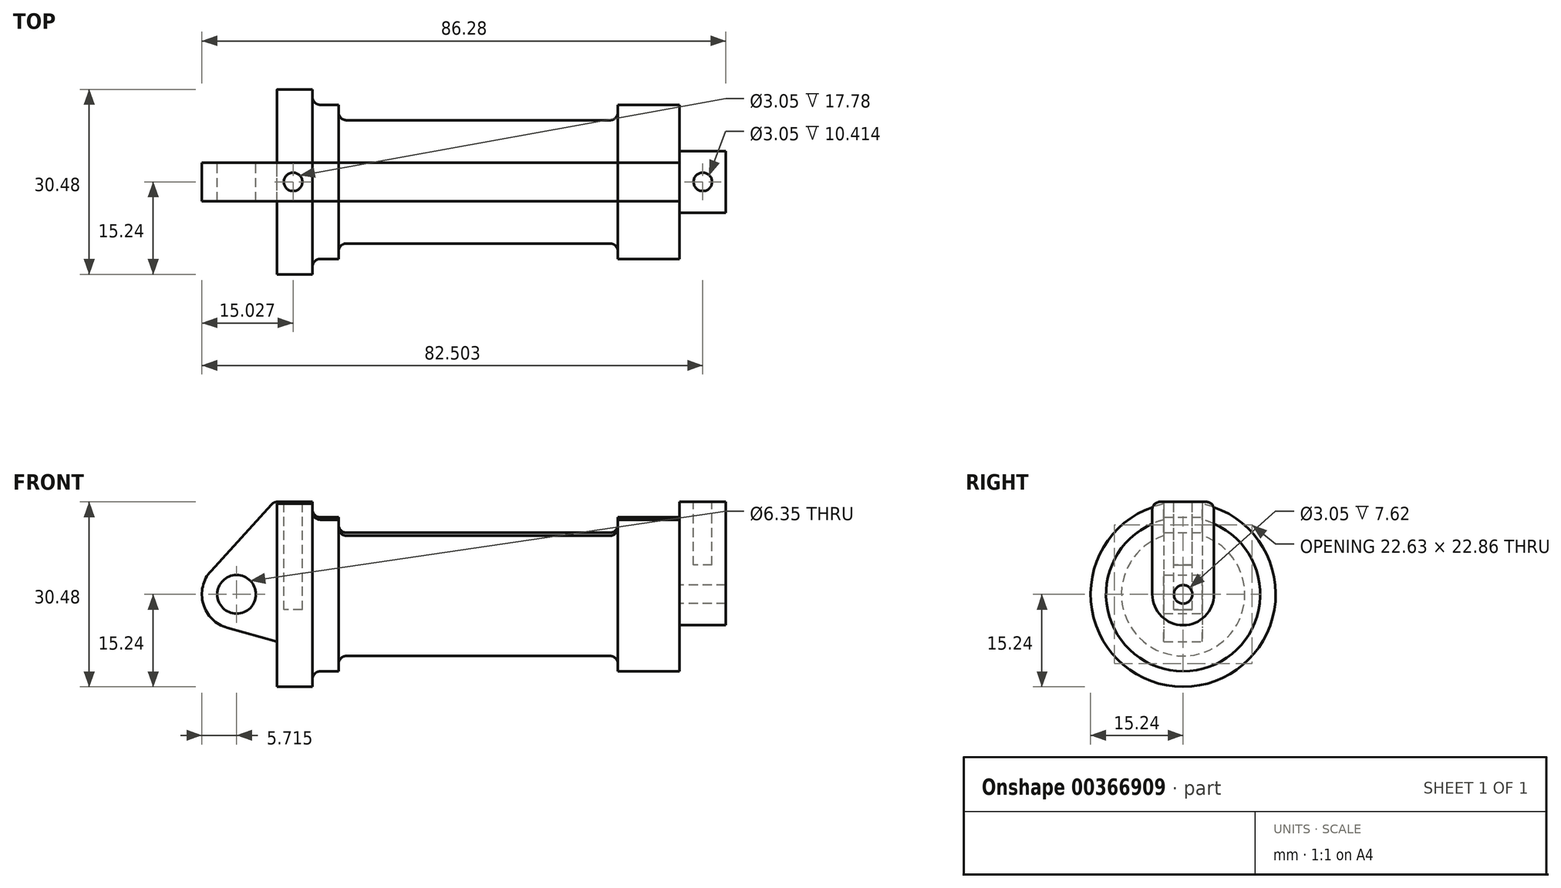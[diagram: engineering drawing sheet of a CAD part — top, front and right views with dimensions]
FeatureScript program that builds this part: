
annotation { "Feature Type Name" : "Feature", "Feature Type Description" : "" }
export const myFeature = defineFeature(function(context is Context, id is Id, definition is map)
    precondition{}
    {
        {
            var Q0;
            Q0=qCreatedBy(makeId("Front.planeOp"),FACE);
            var sketch = newSketch(context, id + "F0", { "sketchPlane" : qUnion([Q0])});
            skLineSegment(sketch, "E0", {"start": v(0, 0) * mm, "end": v(0, 15.25) * mm});
            skLineSegment(sketch, "E1", {"start": v(7.11, 12.7) * mm, "end": v(10.16, 12.7) * mm});
            skLineSegment(sketch, "E2", {"start": v(10.16, 12.7) * mm, "end": v(10.16, 11.43) * mm});
            skLineSegment(sketch, "E3", {"start": v(11.43, 10.16) * mm, "end": v(54.86, 10.16) * mm});
            skLineSegment(sketch, "E4", {"start": v(56.13, 11.43) * mm, "end": v(56.13, 12.7) * mm});
            skLineSegment(sketch, "E5", {"start": v(56.13, 12.7) * mm, "end": v(66.3, 12.7) * mm});
            skLineSegment(sketch, "E6", {"start": v(66.3, 12.7) * mm, "end": v(66.3, 0) * mm});
            skLineSegment(sketch, "E7", {"start": v(66.3, 0) * mm, "end": v(7.11, 0) * mm});
            skLineSegment(sketch, "E8", {"start": v(5.84, 15.24) * mm, "end": v(0.05, 15.24) * mm});
            skLineSegment(sketch, "E9", {"start": v(-0.89, 14.83) * mm, "end": v(-10.88, 3.85) * mm});
            skLineSegment(sketch, "E10", {"start": v(0, 0) * mm, "end": v(-6.65, 0) * mm});
            skCircle(sketch, "E11", {"center": v(-6.65, 0) * mm, "radius": 5.72 * mm});
            skCircle(sketch, "E12", {"center": v(-6.65, 0) * mm, "radius": 3.18 * mm});
            skLineSegment(sketch, "E13", {"start": v(5.84, 15.24) * mm, "end": v(5.84, 13.97) * mm});
            skLineSegment(sketch, "E14", {"start": v(4.23, -8.95) * mm, "end": v(-8.18, -5.5) * mm});
            skPoint(sketch, "E15.newPointA", {"position": v(5.84, -9.4) * mm});
            skPoint(sketch, "E16.visualSharp", {"position": v(10.16, 10.16) * mm});
            skLineSegment(sketch, "E17", {"start": v(5.84, -7.73) * mm, "end": v(5.84, -1.27) * mm});
            skPoint(sketch, "E18.visualSharp", {"position": v(5.84, 12.7) * mm});
            skArc(sketch, "E18.filletArc", {"start": v(5.84, 13.97) * mm, "mid": v(6.21, 13.07) * mm, "end": v(7.11, 12.7) * mm});
            skArc(sketch, "E19.filletArc", {"start": v(10.16, 11.43) * mm, "mid": v(10.53, 10.53) * mm, "end": v(11.43, 10.16) * mm});
            skArc(sketch, "E20.filletArc", {"start": v(7.11, 0) * mm, "mid": v(6.21, -0.37) * mm, "end": v(5.84, -1.27) * mm});
            skPoint(sketch, "E21.visualSharp", {"position": v(56.13, 10.16) * mm});
            skArc(sketch, "E21.filletArc", {"start": v(54.86, 10.16) * mm, "mid": v(55.76, 10.53) * mm, "end": v(56.13, 11.43) * mm});
            skLineSegment(sketch, "E22", {"start": v(7.11, 0) * mm, "end": v(0, 0) * mm});
            skArc(sketch, "E23.filletArc", {"start": v(4.23, -8.95) * mm, "mid": v(5.34, -8.74) * mm, "end": v(5.84, -7.73) * mm});
            skPoint(sketch, "E24.visualSharp", {"position": v(-0.5, 15.24) * mm});
            skArc(sketch, "E24.filletArc", {"start": v(0.05, 15.24) * mm, "mid": v(-0.46, 15.13) * mm, "end": v(-0.89, 14.83) * mm});
            skSolve(sketch);
        }
        {
            var Q0;
            Q0=makeQuery(id+"F0.imprint","IMPRINT",FACE,{"disambiguationData":[TD([[makeQuery(id+"F0.imprint","IMPRINT",EDGE,{"derivedFrom":sQuery(id+"F0.wireOp",EDGE,"E1")}),-1.0]])]});
            var Q1;
            Q1=sQuery(id+"F0.wireOp",EDGE,"E7");
            revolve(context, id + "F1", {"entities" : qUnion([Q0]), "axis" : qUnion([Q1]), "revolveType" : RevolveType.FULL});
        }
        {
            var Q0;
            {var subQ1=sQuery(id+"F0.wireOp",EDGE,"E0");Q0=makeQuery(id+"F0.imprint","IMPRINT",FACE,{"disambiguationData":[TD([[makeQuery(id+"F0.imprint","IMPRINT",EDGE,{"derivedFrom":subQ1}),1.0]])]});}
            var Q1;
            {var subQ0=sQuery(id+"F0.wireOp",EDGE,"E0");Q1=makeQuery(id+"F0.imprint","IMPRINT",FACE,{"disambiguationData":[TD([[makeQuery(id+"F0.imprint","IMPRINT",EDGE,{"derivedFrom":subQ0}),-1.0]])]});}
            var Q2;
            {var subQ0=sQuery(id+"F0.wireOp",EDGE,"E14");Q2=makeQuery(id+"F0.imprint","IMPRINT",FACE,{"disambiguationData":[TD([[makeQuery(id+"F0.imprint","IMPRINT",EDGE,{"derivedFrom":subQ0}),-1.0]])]});}
            var Q3;
            {var subQ5=sQuery(id+"F0.wireOp",EDGE,"E12");Q3=makeQuery(id+"F0.imprint","IMPRINT",FACE,{"disambiguationData":[TD([[makeQuery(id+"F0.imprint","IMPRINT",EDGE,{"derivedFrom":subQ5}),-1.0]])]});}
            extrude(context, id + "F2", {"entities" : qUnion([Q0, Q1, Q2, Q3]), "operationType" : NewBodyOperationType.ADD, "endBound" : BoundingType.SYMMETRIC, "depth" : 6.35 * mm});
        }
        {
            var Q0;
            Q0=makeQuery(id+"F1.opRevolve","SWEPT_FACE",FACE,{"disambiguationData":[OSD([sQuery(id+"F0.wireOp",EDGE,"E6")])]});
            var sketch = newSketch(context, id + "F3", { "sketchPlane" : qUnion([Q0])});
            skCircle(sketch, "E25", {"center": v(0, 0) * mm, "radius": 1.52 * mm});
            skCircle(sketch, "E26", {"center": v(0, 0) * mm, "radius": 5.08 * mm});
            skLineSegment(sketch, "E27", {"start": v(-5.08, 0) * mm, "end": v(-5.08, 13.97) * mm});
            skLineSegment(sketch, "E28", {"start": v(5.08, 0) * mm, "end": v(5.08, 13.97) * mm});
            skLineSegment(sketch, "E29", {"start": v(-3.81, 15.24) * mm, "end": v(3.81, 15.24) * mm});
            skPoint(sketch, "E30.visualSharp", {"position": v(-5.08, 15.24) * mm});
            skArc(sketch, "E30.filletArc", {"start": v(-3.81, 15.24) * mm, "mid": v(-4.7, 14.87) * mm, "end": v(-5.08, 13.97) * mm});
            skPoint(sketch, "E31.visualSharp", {"position": v(5.08, 15.24) * mm});
            skArc(sketch, "E31.filletArc", {"start": v(5.08, 13.97) * mm, "mid": v(4.7, 14.87) * mm, "end": v(3.81, 15.24) * mm});
            skSolve(sketch);
        }
        {
            var Q0;
            Q0 = qSketchRegion(id + "F3", true);
            extrude(context, id + "F4", {"entities" : qUnion([Q0]), "operationType" : NewBodyOperationType.ADD, "depth" : 7.62 * mm});
        }
        {
            var Q0;
            Q0=makeQuery(id+"F2.opExtrude","SWEPT_FACE",FACE,{"disambiguationData":[OSD([sQuery(id+"F0.wireOp",EDGE,"E8")])]});
            var sketch = newSketch(context, id + "F5", { "sketchPlane" : qUnion([Q0])});
            skCircle(sketch, "E32", {"center": v(2.66, 0) * mm, "radius": 1.52 * mm});
            skPoint(sketch, "E32.centerSnap0", {"position": v(5.84, 0) * mm});
            skSolve(sketch);
        }
        {
            var Q0;
            Q0=makeQuery(id+"F5.imprint","IMPRINT",FACE,{"disambiguationData":[TD([[makeQuery(id+"F5.imprint","IMPRINT",EDGE,{"derivedFrom":sQuery(id+"F5.wireOp",EDGE,"E32")}),1.0]])]});
            var Q1;
            Q1=sQuery(id+"F5.wireOp",EDGE,"E32");
            extrude(context, id + "F6", {"entities" : qUnion([Q0]), "operationType" : NewBodyOperationType.REMOVE, "surfaceEntities" : qUnion([Q1]), "oppositeDirection" : true, "depth" : 17.78 * mm});
        }
        {
            var Q0;
            Q0=makeQuery(id+"F4.opExtrude","SWEPT_FACE",FACE,{"disambiguationData":[OSD([sQuery(id+"F3.wireOp",EDGE,"E29")])]});
            var sketch = newSketch(context, id + "F7", { "sketchPlane" : qUnion([Q0])});
            skCircle(sketch, "E33", {"center": v(70.13, 0) * mm, "radius": 1.52 * mm});
            skPoint(sketch, "E33.centerSnap0", {"position": v(66.3, 0) * mm});
            skSolve(sketch);
        }
        {
            var Q0;
            Q0=makeQuery(id+"F7.imprint","IMPRINT",FACE,{"disambiguationData":[TD([[makeQuery(id+"F7.imprint","IMPRINT",EDGE,{"derivedFrom":sQuery(id+"F7.wireOp",EDGE,"E33")}),1.0]])]});
            var Q1;
            Q1=sQuery(id+"F7.wireOp",EDGE,"E33");
            extrude(context, id + "F8", {"entities" : qUnion([Q0]), "operationType" : NewBodyOperationType.REMOVE, "surfaceEntities" : qUnion([Q1]), "oppositeDirection" : true, "depth" : 10.4 * mm});
        }
    });
